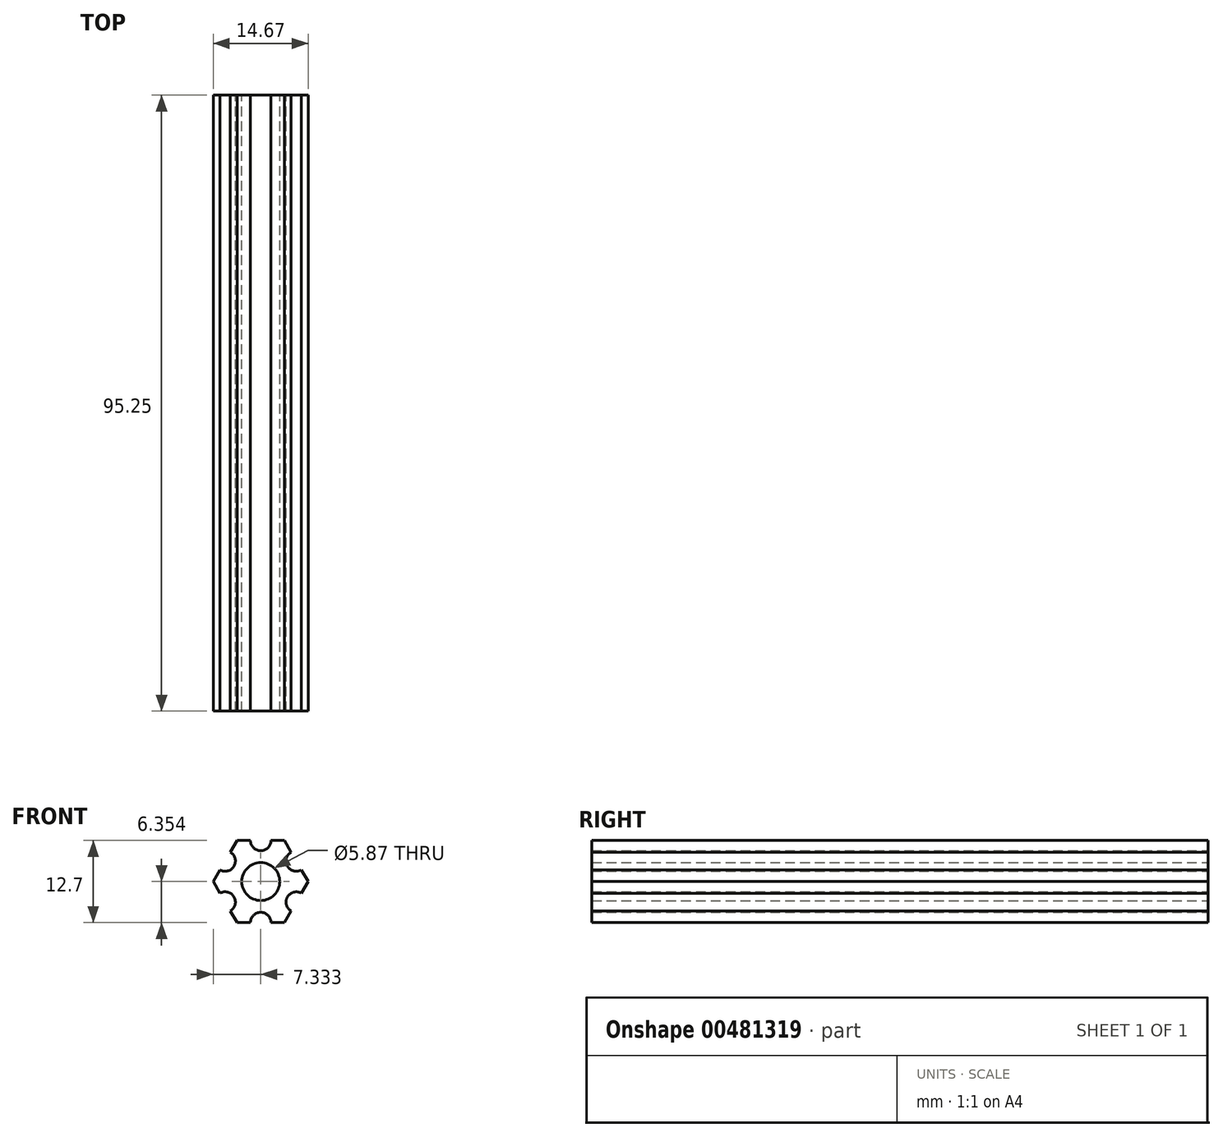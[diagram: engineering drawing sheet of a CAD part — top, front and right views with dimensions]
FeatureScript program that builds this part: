
annotation { "Feature Type Name" : "Feature", "Feature Type Description" : "" }
export const myFeature = defineFeature(function(context is Context, id is Id, definition is map)
    precondition{}
    {
        {
            var Q0;
            Q0=qCreatedBy(makeId("Front.planeOp"),FACE);
            var sketch = newSketch(context, id + "F0", { "sketchPlane" : qUnion([Q0])});
            skLineSegment(sketch, "E0.0.0", {"start": v(6.4, -0.9) * mm, "end": v(7.45, 0.9) * mm});
            skLineSegment(sketch, "E0.0.1", {"start": v(7.45, 0.9) * mm, "end": v(6.4, 2.7) * mm});
            skArc(sketch, "E0.0.2", {"start": v(6.4, 2.7) * mm, "mid": v(4.24, 3.29) * mm, "end": v(4.82, 5.45) * mm});
            skLineSegment(sketch, "E0.0.3", {"start": v(4.82, 5.45) * mm, "end": v(3.78, 7.25) * mm});
            skLineSegment(sketch, "E0.0.4", {"start": v(3.78, 7.25) * mm, "end": v(1.7, 7.25) * mm});
            skArc(sketch, "E0.0.5", {"start": v(1.7, 7.25) * mm, "mid": v(0.11, 5.67) * mm, "end": v(-1.47, 7.25) * mm});
            skLineSegment(sketch, "E0.0.6", {"start": v(-1.47, 7.25) * mm, "end": v(-3.55, 7.25) * mm});
            skLineSegment(sketch, "E0.0.7", {"start": v(-3.55, 7.25) * mm, "end": v(-4.6, 5.45) * mm});
            skArc(sketch, "E0.0.8", {"start": v(-4.6, 5.45) * mm, "mid": v(-4.01, 3.29) * mm, "end": v(-6.18, 2.7) * mm});
            skLineSegment(sketch, "E0.0.9", {"start": v(-6.18, 2.7) * mm, "end": v(-7.22, 0.9) * mm});
            skLineSegment(sketch, "E0.0.10", {"start": v(-7.22, 0.9) * mm, "end": v(-6.18, -0.9) * mm});
            skArc(sketch, "E0.0.11", {"start": v(-6.18, -0.9) * mm, "mid": v(-4.01, -1.48) * mm, "end": v(-4.6, -3.65) * mm});
            skLineSegment(sketch, "E0.0.12", {"start": v(-4.6, -3.65) * mm, "end": v(-3.55, -5.45) * mm});
            skLineSegment(sketch, "E0.0.13", {"start": v(-3.55, -5.45) * mm, "end": v(-1.47, -5.45) * mm});
            skArc(sketch, "E0.0.14", {"start": v(-1.47, -5.45) * mm, "mid": v(0.11, -3.86) * mm, "end": v(1.7, -5.45) * mm});
            skLineSegment(sketch, "E0.0.15", {"start": v(1.7, -5.45) * mm, "end": v(3.78, -5.45) * mm});
            skLineSegment(sketch, "E0.0.16", {"start": v(3.78, -5.45) * mm, "end": v(4.82, -3.65) * mm});
            skArc(sketch, "E0.0.17", {"start": v(4.82, -3.65) * mm, "mid": v(4.24, -1.48) * mm, "end": v(6.4, -0.9) * mm});
            skCircle(sketch, "E1.0", {"center": v(0.11, 0.9) * mm, "radius": 2.93 * mm});
            skSolve(sketch);
        }
        {
            var Q0;
            Q0=makeQuery(id+"F0.imprint","IMPRINT",FACE,{"disambiguationData":[TD([[makeQuery(id+"F0.imprint","IMPRINT",EDGE,{"derivedFrom":sQuery(id+"F0.wireOp",EDGE,"E0.0.0")}),1.0]])]});
            extrude(context, id + "F1", {"entities" : qUnion([Q0]), "depth" : 95.25 * mm, "offsetDistance" : 25.4 * mm});
        }
    });
